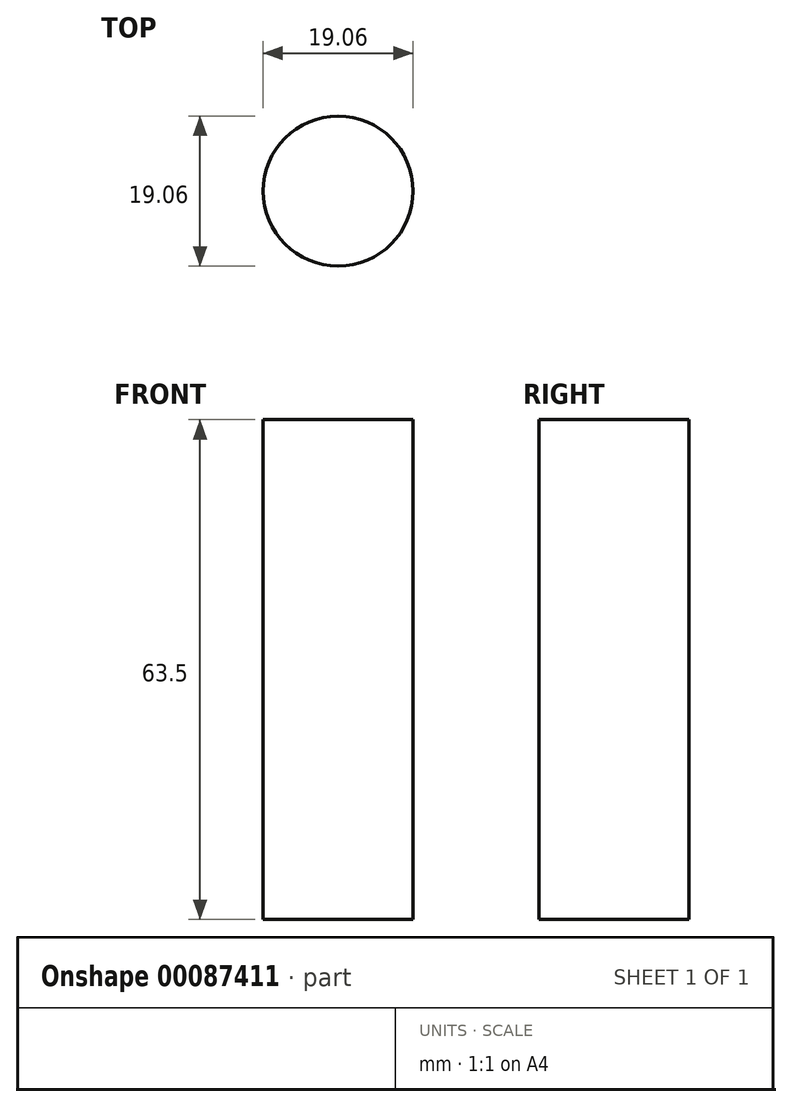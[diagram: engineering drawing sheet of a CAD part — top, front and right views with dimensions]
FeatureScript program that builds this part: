
annotation { "Feature Type Name" : "Feature", "Feature Type Description" : "" }
export const myFeature = defineFeature(function(context is Context, id is Id, definition is map)
    precondition{}
    {
        {
            var Q0;
            Q0=qCreatedBy(makeId("Top.planeOp"),FACE);
            var sketch = newSketch(context, id + "F0", { "sketchPlane" : qUnion([Q0])});
            skCircle(sketch, "E0", {"center": v(0, 0) * mm, "radius": 9.53 * mm});
            skSolve(sketch);
        }
        {
            var Q0;
            Q0 = qSketchRegion(id + "F0", true);
            extrude(context, id + "F1", {"entities" : qUnion([Q0]), "depth" : 63.5 * mm});
        }
    });
